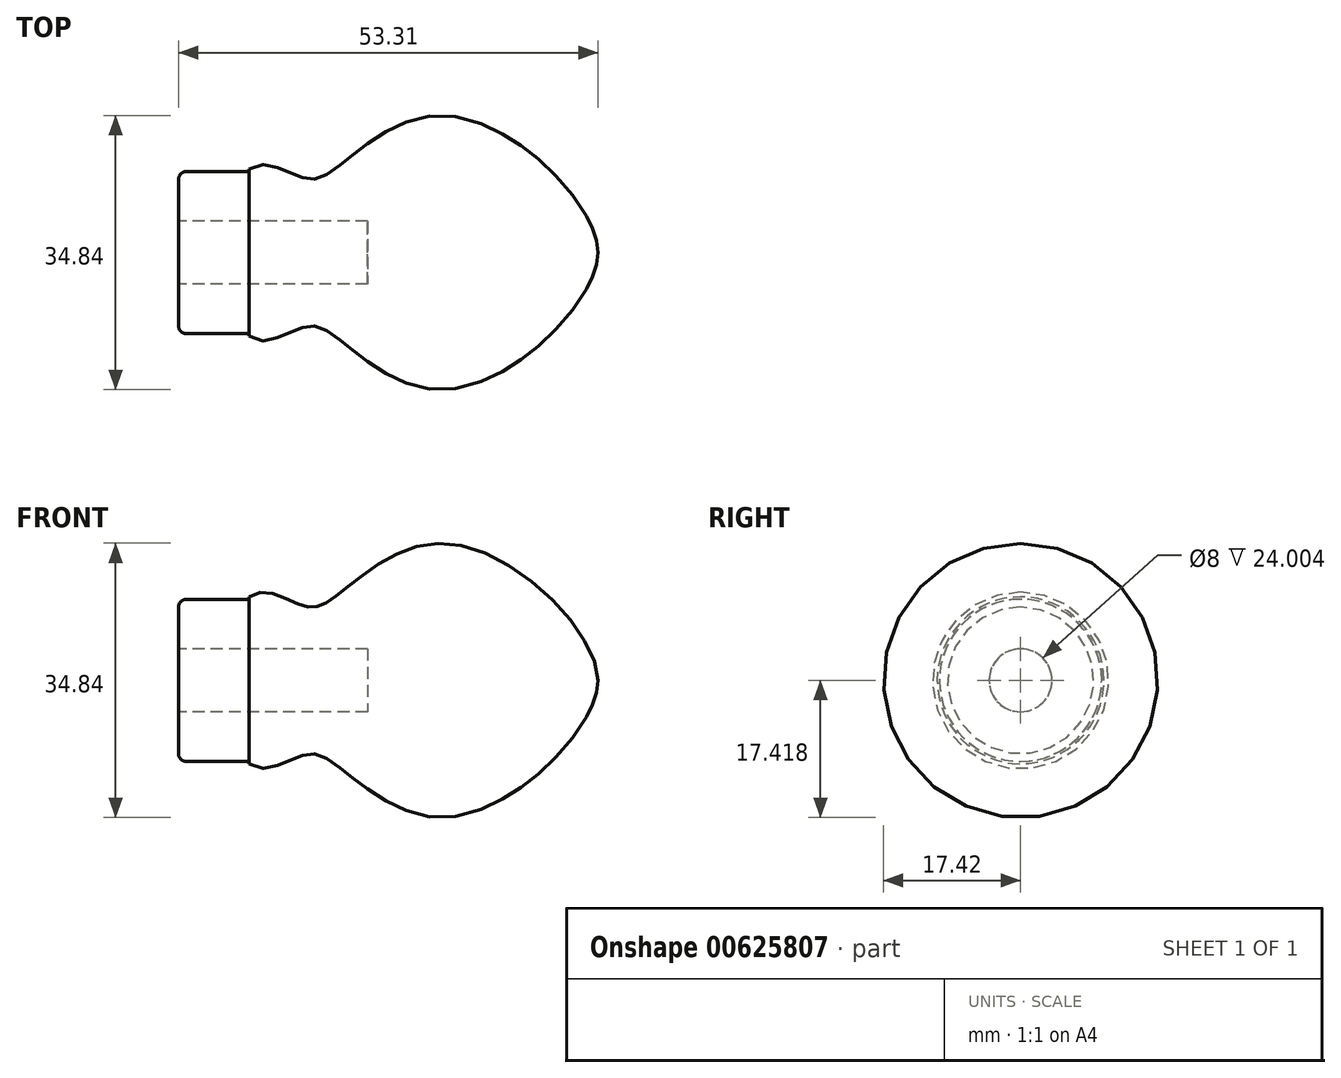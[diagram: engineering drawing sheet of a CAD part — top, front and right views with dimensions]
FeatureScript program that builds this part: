
annotation { "Feature Type Name" : "Feature", "Feature Type Description" : "" }
export const myFeature = defineFeature(function(context is Context, id is Id, definition is map)
    precondition{}
    {
        {
            var Q0;
            Q0=qCreatedBy(makeId("Front.planeOp"),FACE);
            var sketch = newSketch(context, id + "F0", { "sketchPlane" : qUnion([Q0])});
            skLineSegment(sketch, "E0", {"start": v(-42.4, 13.85) * mm, "end": v(-34.42, 13.85) * mm});
            skLineSegment(sketch, "E1", {"start": v(-34.42, 13.85) * mm, "end": v(-34.42, 15.14) * mm});
            skLineSegment(sketch, "E2", {"start": v(-19.4, 4.55) * mm, "end": v(-16.72, 4.55) * mm});
            skLineSegment(sketch, "E3", {"start": v(-16.72, 4.55) * mm, "end": v(9.9, 4.55) * mm});
            skFitSpline(sketch, "E4", {"points": [v(-34.42, 15.14) * mm, v(-27.7, 14.1) * mm, v(-23.74, 15) * mm, v(-8.9, 21.91) * mm, v(9.9, 4.55) * mm], "startDerivative": vector(28.38, 25.56) * mm, "endDerivative": vector(2.02, -52.44) * mm});
            skLineSegment(sketch, "E5", {"start": v(-42.4, 13.85) * mm, "end": v(-42.4, 8.55) * mm});
            skPoint(sketch, "E6", {"position": v(-19.4, 4.55) * mm});
            skLineSegment(sketch, "E7", {"start": v(-19.4, 4.55) * mm, "end": v(-19.4, 8.55) * mm});
            skLineSegment(sketch, "E8", {"start": v(-19.4, 8.55) * mm, "end": v(-42.4, 8.55) * mm});
            skPoint(sketch, "E9.orphan", {"position": v(-42.4, 4.55) * mm});
            skSolve(sketch);
        }
        {
            var Q0;
            Q0=makeQuery(id+"F0.imprint","IMPRINT",FACE,{"disambiguationData":[TD([[makeQuery(id+"F0.imprint","IMPRINT",EDGE,{"derivedFrom":sQuery(id+"F0.wireOp",EDGE,"E0")}),-1.0]])]});
            var Q1;
            Q1=sQuery(id+"F0.wireOp",EDGE,"E3");
            revolve(context, id + "F1", {"entities" : qUnion([Q0]), "axis" : qUnion([Q1]), "revolveType" : RevolveType.FULL});
        }
        {
            var Q0;
            Q0=qCreatedBy(makeId("Right.planeOp"),FACE);
            var Q1;
            Q1=sQuery(id+"F0.wireOp",VERTEX,"E5.end");
            cPlane(context, id + "F2", {"entities" : qUnion([Q0, Q1]), "cplaneType" : CPlaneType.PLANE_POINT, "offset" : 25 * mm, "width" : 150 * mm, "height" : 150 * mm});
        }
        {
            var Q0;
            Q0=qCreatedBy(id+"F2.planeOp",FACE);
            var sketch = newSketch(context, id + "F3", { "sketchPlane" : qUnion([Q0])});
            skCircle(sketch, "E10.0", {"center": v(0, 4.55) * mm, "radius": 9.3 * mm});
            skCircle(sketch, "E11", {"center": v(0, 4.55) * mm, "radius": 10.3 * mm});
            skCircle(sketch, "E12", {"center": v(0, 4.55) * mm, "radius": 4 * mm});
            skSolve(sketch);
        }
        {
            var Q0;
            Q0=makeQuery(id+"F3.imprint","IMPRINT",FACE,{"disambiguationData":[TD([[makeQuery(id+"F3.imprint","IMPRINT",EDGE,{"derivedFrom":sQuery(id+"F3.wireOp",EDGE,"E10.0")}),-1.0]])]});
            var Q1;
            Q1=makeQuery(id+"F1.opRevolve","SWEPT_FACE",FACE,{"disambiguationData":[OSD([sQuery(id+"F0.wireOp",EDGE,"E1")])]});
            extrude(context, id + "F4", {"entities" : qUnion([Q0]), "endBound" : BoundingType.UP_TO_SURFACE, "depth" : 25 * mm, "endBoundEntityFace" : qUnion([Q1]), "offsetDistance" : 25 * mm});
        }
        {
            var Q0;
            Q0=makeQuery(id+"F3.imprint","IMPRINT",FACE,{"disambiguationData":[TD([[makeQuery(id+"F3.imprint","IMPRINT",EDGE,{"derivedFrom":sQuery(id+"F3.wireOp",EDGE,"E10.0")}),1.0]])]});
            var Q1;
            Q1=makeQuery(id+"F3.imprint","IMPRINT",FACE,{"disambiguationData":[TD([[makeQuery(id+"F3.imprint","IMPRINT",EDGE,{"derivedFrom":sQuery(id+"F3.wireOp",EDGE,"E10.0")}),-1.0]])]});
            extrude(context, id + "F5", {"entities" : qUnion([Q0, Q1]), "operationType" : NewBodyOperationType.ADD, "oppositeDirection" : true, "depth" : 1 * mm, "offsetDistance" : 25 * mm});
        }
        {
            var Q0;
            Q0=makeQuery(id+"F5.opExtrude","CAP_EDGE",EDGE,{"disambiguationData":[OSD([sQuery(id+"F3.wireOp",EDGE,"E11")])],"isStart":false});
            fillet(context, id + "F6", {"entities" : qUnion([Q0]), "radius" : 1 * mm, "tangentPropagation" : true, "allowEdgeOverflow" : false});
        }
    });
